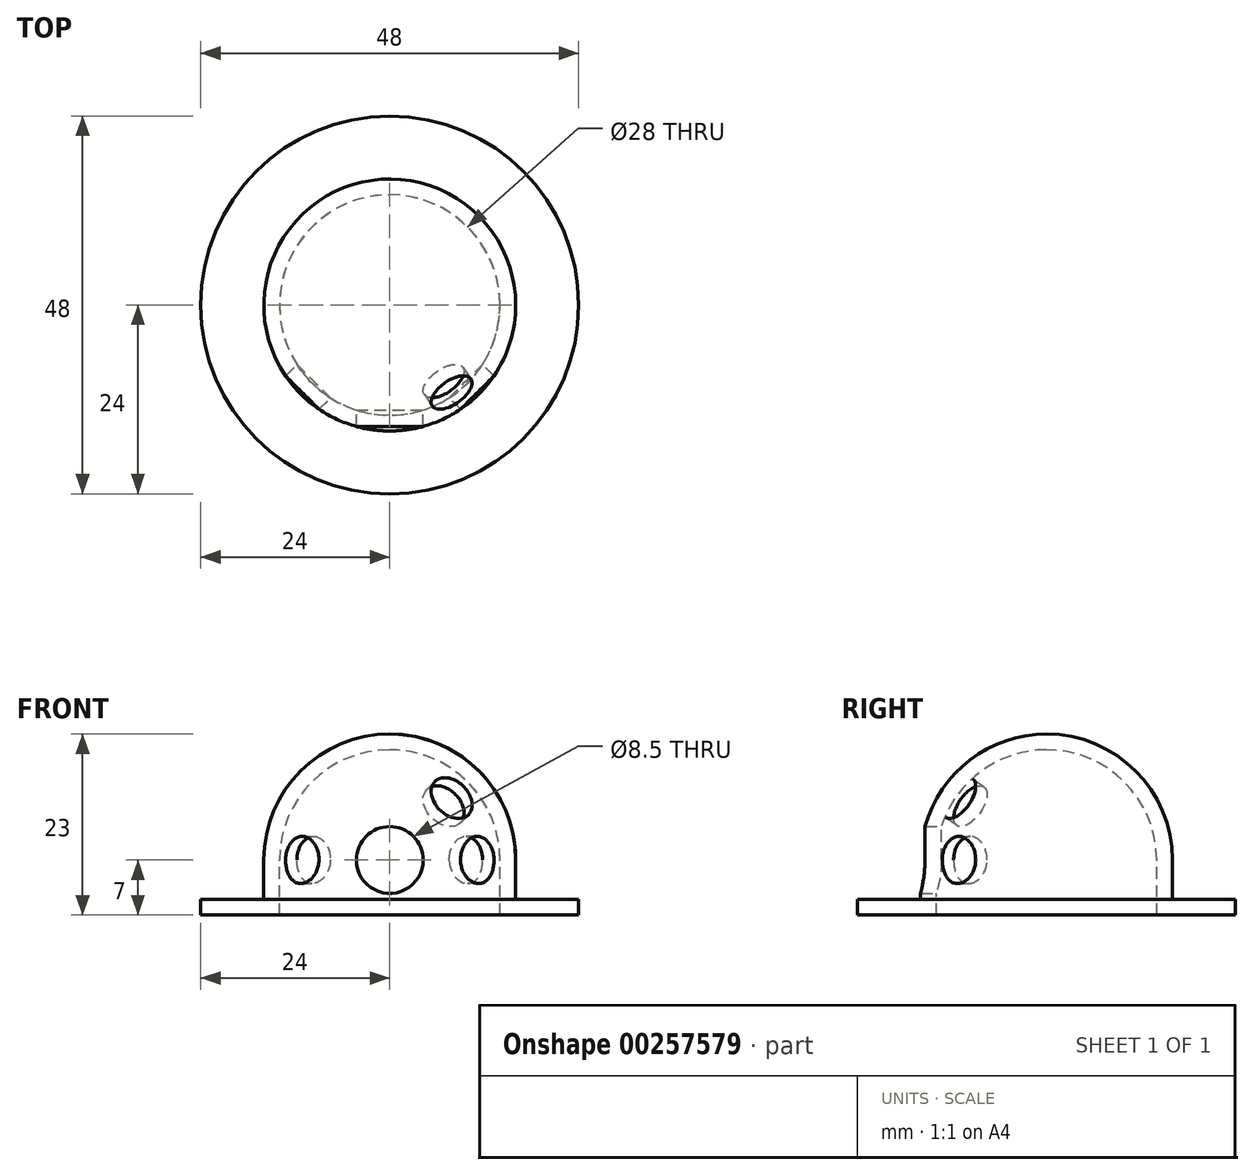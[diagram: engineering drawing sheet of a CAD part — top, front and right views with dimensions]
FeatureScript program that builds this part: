
annotation { "Feature Type Name" : "Feature", "Feature Type Description" : "" }
export const myFeature = defineFeature(function(context is Context, id is Id, definition is map)
    precondition{}
    {
        {
            var Q0;
            Q0=qCreatedBy(makeId("Front.planeOp"),FACE);
            var sketch = newSketch(context, id + "F0", { "sketchPlane" : qUnion([Q0])});
            skLineSegment(sketch, "E0", {"start": v(-14, -7) * mm, "end": v(-24, -7) * mm});
            skLineSegment(sketch, "E1", {"start": v(-24, -7) * mm, "end": v(-24, -5) * mm});
            skLineSegment(sketch, "E2", {"start": v(-24, -5) * mm, "end": v(-16, -5) * mm});
            skLineSegment(sketch, "E3", {"start": v(-16, -5) * mm, "end": v(-16, 0) * mm});
            skLineSegment(sketch, "E4", {"start": v(-14, -7) * mm, "end": v(-14, 0) * mm});
            skArc(sketch, "E5", {"start": v(0, 14) * mm, "mid": v(-9.9, 9.9) * mm, "end": v(-14, 0) * mm});
            skArc(sketch, "E6", {"start": v(0, 16) * mm, "mid": v(-11.31, 11.31) * mm, "end": v(-16, 0) * mm});
            skLineSegment(sketch, "E7", {"start": v(0, 16) * mm, "end": v(0, 14) * mm});
            skSolve(sketch);
        }
        {
            var Q0;
            Q0 = qSketchRegion(id + "F0", true);
            var Q1;
            Q1=sQuery(id+"F0.wireOp",EDGE,"E7");
            revolve(context, id + "F1", {"entities" : qUnion([Q0]), "axis" : qUnion([Q1]), "revolveType" : RevolveType.FULL});
        }
        {
            var Q0;
            Q0=qCreatedBy(makeId("Front.planeOp"),FACE);
            var sketch = newSketch(context, id + "F2", { "sketchPlane" : qUnion([Q0])});
            skCircle(sketch, "E8", {"center": v(0, 0) * mm, "radius": 4.25 * mm});
            skSolve(sketch);
        }
        {
            var Q0;
            Q0 = qSketchRegion(id + "F2", true);
            extrude(context, id + "F3", {"entities" : qUnion([Q0]), "operationType" : NewBodyOperationType.REMOVE, "depth" : 50 * mm});
        }
        {
            var Q0;
            Q0=qCreatedBy(makeId("Top.planeOp"),FACE);
            var sketch = newSketch(context, id + "F4", { "sketchPlane" : qUnion([Q0])});
            skLineSegment(sketch, "E9", {"start": v(-39.11, -39.11) * mm, "end": v(32.62, 32.62) * mm, "construction": true});
            skLineSegment(sketch, "E10", {"start": v(-37.35, 37.35) * mm, "end": v(42.98, -42.98) * mm, "construction": true});
            skSolve(sketch);
        }
        {
            var Q0;
            Q0=sQuery(id+"F4.wireOp",EDGE,"E10");
            cPlane(context, id + "F5", {"entities" : qUnion([Q0]), "cplaneType" : CPlaneType.LINE_ANGLE, "offset" : 25 * mm, "angle" : 90 * degree, "width" : 150 * mm, "height" : 150 * mm});
        }
        {
            var Q0;
            Q0=qCreatedBy(id+"F5.planeOp",FACE);
            var sketch = newSketch(context, id + "F6", { "sketchPlane" : qUnion([Q0])});
            skCircle(sketch, "E11", {"center": v(0, 0) * mm, "radius": 3 * mm});
            skSolve(sketch);
        }
        {
            var Q0;
            Q0 = qSketchRegion(id + "F6", true);
            extrude(context, id + "F7", {"entities" : qUnion([Q0]), "operationType" : NewBodyOperationType.REMOVE, "oppositeDirection" : true, "depth" : 25 * mm});
        }
        {
            var Q0;
            Q0=qCreatedBy(makeId("Front.planeOp"),FACE);
            var sketch = newSketch(context, id + "F8", { "sketchPlane" : qUnion([Q0])});
            skLineSegment(sketch, "E12", {"start": v(0, 0) * mm, "end": v(30.29, 30.29) * mm, "construction": true});
            skLineSegment(sketch, "E13", {"start": v(0, 0) * mm, "end": v(-31.13, 31.13) * mm, "construction": true});
            skSolve(sketch);
        }
        {
            var Q0;
            Q0=sQuery(id+"F8.wireOp",EDGE,"E12");
            cPlane(context, id + "F9", {"entities" : qUnion([Q0]), "cplaneType" : CPlaneType.LINE_ANGLE, "offset" : 25 * mm, "angle" : 90 * degree, "width" : 150 * mm, "height" : 150 * mm});
        }
        {
            var Q0;
            Q0=qCreatedBy(id+"F9.planeOp",FACE);
            var sketch = newSketch(context, id + "F10", { "sketchPlane" : qUnion([Q0])});
            skLineSegment(sketch, "E14", {"start": v(0, 0) * mm, "end": v(19.81, 19.81) * mm, "construction": true});
            skLineSegment(sketch, "E15", {"start": v(16.68, 16.68) * mm, "end": v(14.56, 18.8) * mm});
            skLineSegment(sketch, "E16", {"start": v(14.56, 18.8) * mm, "end": v(1.88, 6.12) * mm});
            skLineSegment(sketch, "E17", {"start": v(1.88, 6.12) * mm, "end": v(4, 4) * mm});
            skLineSegment(sketch, "E18", {"start": v(4, 4) * mm, "end": v(16.68, 16.68) * mm});
            skSolve(sketch);
        }
        {
            var Q0;
            Q0 = qSketchRegion(id + "F10", true);
            var Q1;
            Q1=sQuery(id+"F10.wireOp",EDGE,"E18");
            revolve(context, id + "F11", {"operationType" : NewBodyOperationType.REMOVE, "entities" : qUnion([Q0]), "axis" : qUnion([Q1]), "revolveType" : RevolveType.FULL, "oppositeDirection" : true});
        }
        {
            var Q0;
            Q0=sQuery(id+"F4.wireOp",EDGE,"E9");
            cPlane(context, id + "F12", {"entities" : qUnion([Q0]), "cplaneType" : CPlaneType.LINE_ANGLE, "offset" : 25 * mm, "angle" : 90 * degree, "width" : 150 * mm, "height" : 150 * mm});
        }
        {
            var Q0;
            Q0=qCreatedBy(id+"F12.planeOp",FACE);
            var sketch = newSketch(context, id + "F13", { "sketchPlane" : qUnion([Q0])});
            skCircle(sketch, "E19", {"center": v(0, 0) * mm, "radius": 3 * mm});
            skSolve(sketch);
        }
        {
            var Q0;
            Q0 = qSketchRegion(id + "F13", true);
            extrude(context, id + "F14", {"entities" : qUnion([Q0]), "operationType" : NewBodyOperationType.REMOVE, "depth" : 25 * mm});
        }
        {
            var Q0;
            Q0=sQuery(id+"F8.wireOp",EDGE,"E13");
            cPlane(context, id + "F15", {"entities" : qUnion([Q0]), "cplaneType" : CPlaneType.LINE_ANGLE, "offset" : 25 * mm, "angle" : 90 * degree, "width" : 150 * mm, "height" : 150 * mm});
        }
    });
